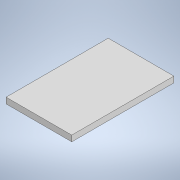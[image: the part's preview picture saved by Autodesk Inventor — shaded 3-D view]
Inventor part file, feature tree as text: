
AUTODESK INVENTOR PART (.ipt)
format: ipt  version: 2020 (Build 240168000, 168)  size: 91,648 bytes
history: native  units: in
note: dims shown in document units (in); Inventor stores cm internally (conversion verified against a paired STEP export)
features: extrude x1, sketch x1
ambient origin geometry x8: Origin, YZ Plane, XZ Plane, XY Plane, X Axis, Y Axis, Z Axis, Center Point
bodies: Solid1 (feature_tree)
feature tree (2):
  extrude  "Extrusion1"  Depth=1.7717in
  sketch  "Sketch1"  dims[d0=2.7559in d1=1.7717in d2=0.8858in d3=1.378in d4=0.1575in d5=0.0in]
